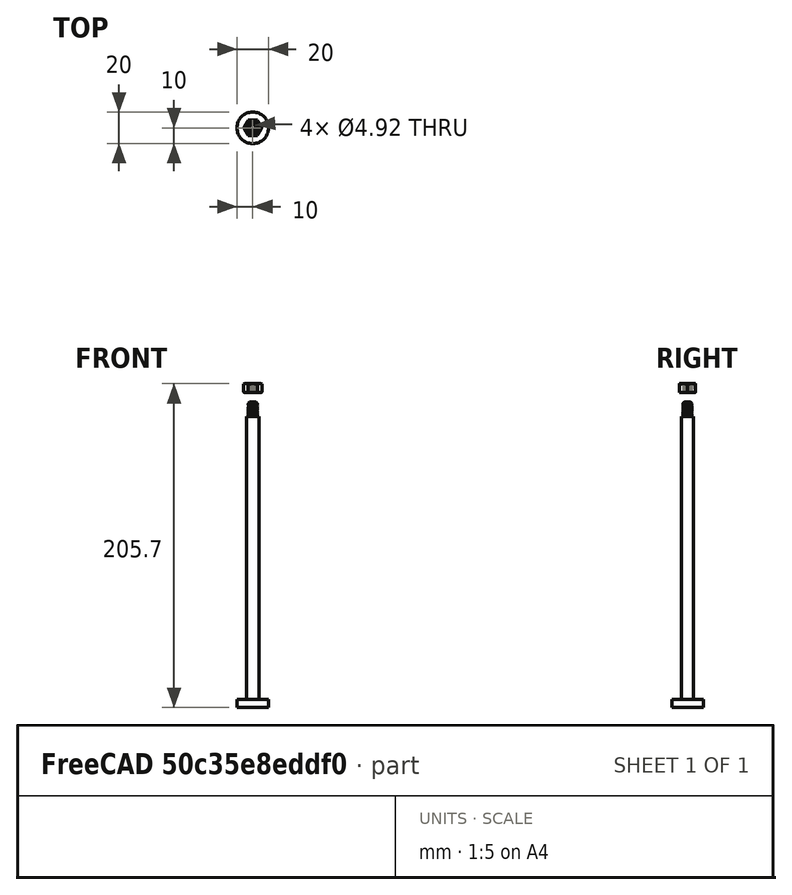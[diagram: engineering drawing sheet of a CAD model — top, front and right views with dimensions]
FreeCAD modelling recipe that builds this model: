
FCSTD DOCUMENT  (FreeCAD 0.21R33771 (Git))
Label: rod
License: All rights reserved
LicenseURL: https://en.wikipedia.org/wiki/All_rights_reserved
objects: Part::Cylinder×2, Part::FeaturePython×2, Part::Fuse×1
note: 5 computed .brp shape members not serialized (recipe doc carries the construction recipe); baked Part::Feature solids carry a one-line shape summary decoded from their .brp

FEATURE [Part::Cylinder] Cylinder
  Angle = 360
  AttacherType = Attacher::AttachEngine3D
  FirstAngle = 0
  Height = 180
  Radius = 3.9
  SecondAngle = 0
FEATURE [Part::Cylinder] Cylinder001
  Angle = 360
  AttacherType = Attacher::AttachEngine3D
  FirstAngle = 0
  Height = 5
  Placement = pos=(0,0,-5) rot=(0,0,1;0rad)
  Radius = 10
  SecondAngle = 0
FEATURE [Part::FeaturePython] ThreadedRod  label="M6x10-ThreadedRod"  # Fasteners workbench fastener (typed FeaturePython)
  Placement = pos=(0,0,189) rot=(0,0,1;0rad)
  diameter = 8
  diameterCustom = 6
  invert = false
  leftHanded = false
  length = 10
  matchOuter = false
  offset = 0
  pitchCustom = 1
  thread = true
  type = 4
FEATURE [Part::Fuse] Fusion
  Base = -> Cylinder
  Tool = -> ThreadedRod
FEATURE [Part::FeaturePython] Nut001  label="M6-Nut"  # Fasteners workbench fastener (typed FeaturePython)
  Placement = pos=(0,0,195) rot=(0,0,1;0rad)
  diameter = 2
  invert = false
  leftHanded = false
  matchOuter = false
  offset = 0
  thread = true
  type = 26
